# Revit family: SETI-CRS
name_source: partatom
category: Lighting Fixtures
revit_build: Autodesk Revit 2014 (Build: 20130308_1515(x64)
units: mm (PartAtom-declared; Revit-internal decimal feet)

## types (1)
- SETI
    Apparent Load = 55 VA
    Assembly Code = D5020280
    CRI = 70
    Certification = CSA certified to UL 1598, UL 8750, CSA
C22.2 No. 250.0-08, and CSA C22.2 No.
250.13-14.
    Color Filter = 16777215
    Controls = dimming, timed dimming with simple delay,
or timed dimming by time of night
    Default Elevation = 48 "
    Description = The energy efficiency of LED lighting becomes an architectural statement with this high performance luminaire. A wide range of top shade options offers the architect a design solution to complement its setting while energy efficiency is achieved to meet the requirements of a LEED certified design. As a NO Glare indirect LED lighting fixture, the SETI is ideal as for walkways, atriums, exterior and interior applications with high pedestrian traffic.
    Dimming Lamp Color Temperature Shift = <None>
    Emit Shape Visible in Rendering = No
    Emit from Circle Diameter = 10 "
    Finish = Hubbell-Matte Black
    Glass = Hubbell-Matte Black
    IP Rating = IP55
    Lamp = LED
    Light Distribution = IES Type II,III,IV
    Lighting Connector Description = Lighting Connector
    Load Classification = Lighting
    Manufacturer = Beacon
    Model = SETI
    Model Type = Single fixture
    Photometric Web File = SETI-24L-55-3K7-30RD.ies
    Power Factor = 1
    Product Documentation Link = https://hubbellcdn.com
    Product Page URL = https://www.hubbell.com
    Tilt Angle = -90.00°
    Type Comments = Light Fixture
    URL = https://www.hubbell.com
    Voltage = 120 V
    Warranty = 5 Year Limited Warranty
    Wattage Comments = 55W
    Watts = 55 W

## geometry (parser evidence)
native form markers: Blend x40, Sweep x1
no freeform markers — native parametric forms only
